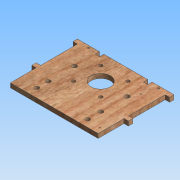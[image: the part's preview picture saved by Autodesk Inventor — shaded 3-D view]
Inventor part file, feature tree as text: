
AUTODESK INVENTOR PART (.ipt)
format: ipt  version: 2015 (Build 190159000, 159)  size: 296,448 bytes
history: native  units: mm
features: sketch x10, extrude x9, other x5, hole x3, projected_geometry x2, reference x2
ambient origin geometry x8: Origin, YZ Plane, XZ Plane, XY Plane, X Axis, Y Axis, Z Axis, Center Point
bodies: Body1 (feature_tree)
feature tree (31):
  other  "Blocks"
  extrude  "Extrusion2"  Depth=50.0mm
  hole  "Hole4"  [1 undecoded]
  hole  "Hole5"  [1 undecoded]
  hole  "Hole8"  [1 undecoded]
  extrude  "Extrusion11"  Depth=5.0mm
  extrude  "Extrusion12"  Depth=60.0mm
  extrude  "Extrusion13"  Depth=30.0mm
  sketch  "Sketch47"  dims[d78=22.0mm d79=6.0mm d80=4.0mm d81=2.0mm d82=90.0deg d83=2.0mm d84=0.0mm d176=28.0mm]
  extrude  "Extrusion14"  Depth=1.0mm
  extrude  "Extrusion15"  Depth=5.0mm
  extrude  "Extrusion16"  Depth=5.0mm TaperAngle=0.0deg
  extrude  "Extrusion17"  Depth=5.0mm TaperAngle=0.0deg
  extrude  "Extrusion18"  Depth=47.0mm
  sketch  "Sketch13"  dims[d21=100.0mm d22=50.0mm]
  sketch  "Sketch16"  dims[d23=5.0mm d24=0.0mm d43=31.0mm]
  sketch  "Sketch17"  dims[d44=31.0mm]
  other  "Block1"
  other  "Block2"
  other  "Block3"
  other  "Block4"
  projected_geometry  "Projected Loop3"
  sketch  "Sketch45"  dims[d45=4.0mm d46=6.0mm d47=4.0mm d48=2.0mm d49=90.0deg d50=4.0mm d51=0.0mm d52=60.0mm]
  projected_geometry  "Projected Loop4"
  reference  "Reference1"
  reference  "Reference2"
  sketch  "Sketch46"  dims[d53=5.2mm d54=6.0mm d55=4.0mm d56=2.0mm d57=90.0deg d58=4.0mm d59=0.0mm]
  sketch  "Sketch48"  dims[d179=5.0mm d184=5.0mm]
  sketch  "Sketch49"  dims[d185=8.0mm d189=60.0mm]
  sketch  "Sketch50"  dims[d190=30.0mm d191=8.0mm]
  sketch  "Sketch51"  dims[d192=5.0mm d193=15.0mm d196=5.0mm d197=5.0mm d198=0.0mm d200=5.0mm d201=0.0mm d202=47.0mm d203=5.0mm d204=5.0mm d205=20.0mm d206=5.0mm d207=5.0mm d208=20.0mm d209=10.0mm d210=0.0mm d211=2.0mm d212=2.5mm d213=10.0mm d214=2.0mm d215=10.0mm d216=2.5mm d217=10.0mm d218=0.0mm d219=10.0mm d220=0.0mm d221=5.0mm d222=5.0mm d223=5.0mm d224=5.0mm d225=5.0mm d226=0.0mm d227=5.0mm d228=5.0mm d229=47.0mm d230=5.0mm d231=0.0mm d232=5.0mm d233=5.0mm d234=47.0mm d235=5.0mm d236=0.0mm d29=1.0mm d30=1.0mm]
note: 3 required parameter values undecoded (feature->parameter linkage not recoverable at this tier; creation-order binding heuristic only, values carry confidence <= 0.55)
